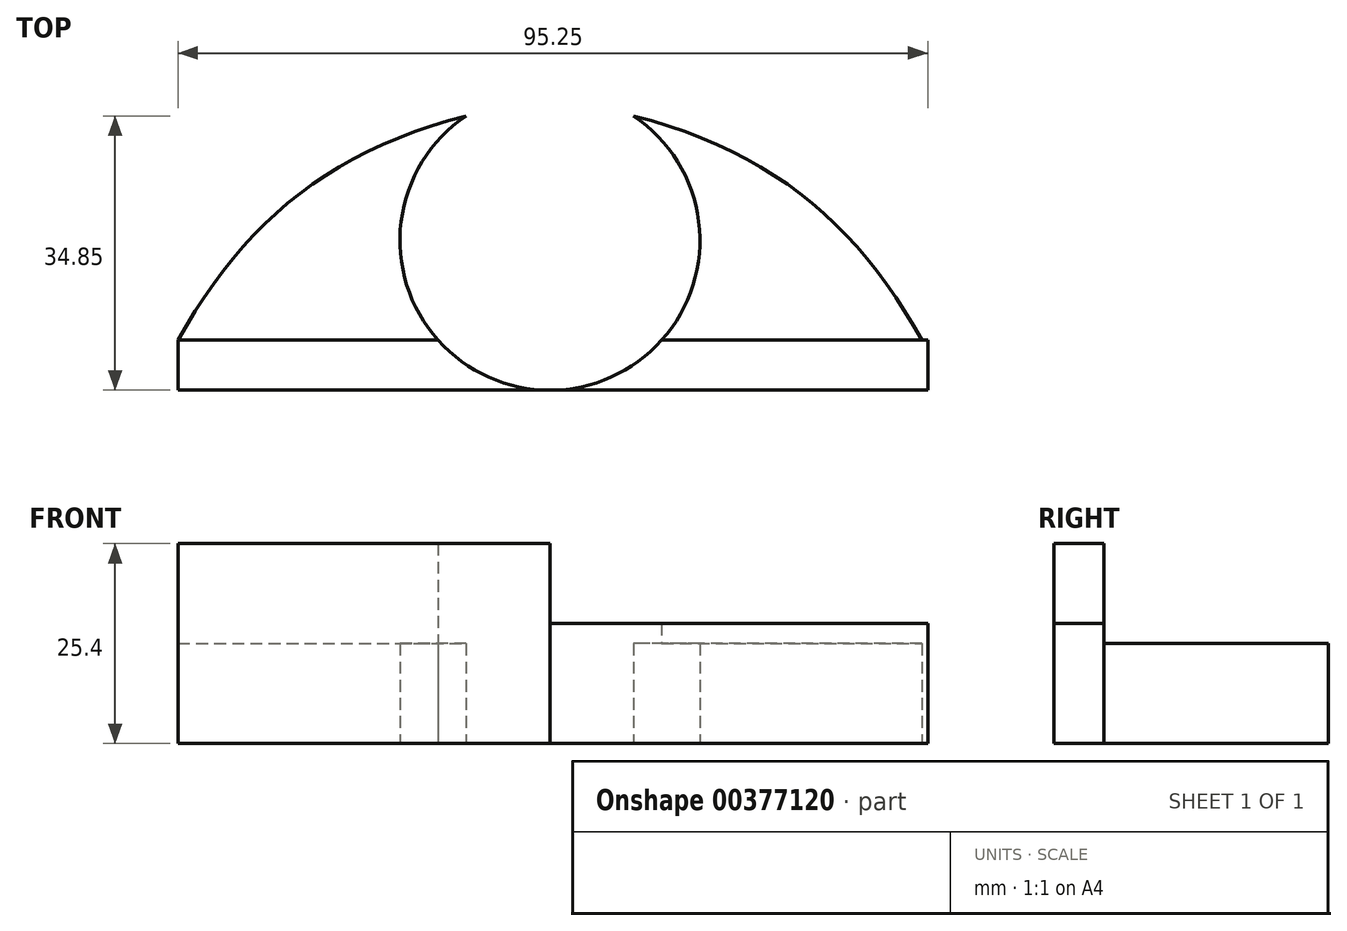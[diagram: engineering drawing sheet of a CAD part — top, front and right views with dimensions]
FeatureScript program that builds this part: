
annotation { "Feature Type Name" : "Feature", "Feature Type Description" : "" }
export const myFeature = defineFeature(function(context is Context, id is Id, definition is map)
    precondition{}
    {
        {
            var Q0;
            Q0=qCreatedBy(makeId("Top.planeOp"),FACE);
            var sketch = newSketch(context, id + "F0", { "sketchPlane" : qUnion([Q0])});
            skArc(sketch, "E0", {"start": v(-10.64, 15.8) * mm, "mid": v(0, -19.05) * mm, "end": v(10.64, 15.8) * mm});
            skLineSegment(sketch, "E1.bottom", {"start": v(-47.24, -12.7) * mm, "end": v(-14.2, -12.7) * mm});
            skLineSegment(sketch, "E1.top", {"start": v(-47.24, -19.05) * mm, "end": v(0, -19.05) * mm});
            skLineSegment(sketch, "E1.left", {"start": v(-47.24, -12.7) * mm, "end": v(-47.24, -19.05) * mm});
            skLineSegment(sketch, "E1.right", {"start": v(48.01, -12.7) * mm, "end": v(48.01, -19.05) * mm});
            skLineSegment(sketch, "E2.trimOffspring", {"start": v(14.2, -12.7) * mm, "end": v(48.01, -12.7) * mm});
            skLineSegment(sketch, "E3", {"start": v(0, -19.05) * mm, "end": v(48.01, -19.05) * mm});
            skLineSegment(sketch, "E4", {"start": v(-29.77, 12.78) * mm, "end": v(29.48, 12.78) * mm, "construction": true});
            skLineSegment(sketch, "E5", {"start": v(0, -23.19) * mm, "end": v(0, 34.86) * mm, "construction": true});
            skFitSpline(sketch, "E6", {"points": [v(-47.24, -12.7) * mm, v(-10.64, 15.8) * mm], "startDerivative": vector(24.24, 43.74) * mm, "endDerivative": vector(52.98, 13.61) * mm});
            skFitSpline(sketch, "E7.MirrorCS", {"points": [v(47.24, -12.7) * mm, v(10.64, 15.8) * mm], "startDerivative": vector(-24.24, 43.74) * mm, "endDerivative": vector(-52.98, 13.61) * mm});
            skLineSegment(sketch, "E8.bottom", {"start": v(-47.24, -19.05) * mm, "end": v(-104, -19.05) * mm});
            skLineSegment(sketch, "E8.top", {"start": v(-47.24, -12.5) * mm, "end": v(-104, -12.5) * mm});
            skLineSegment(sketch, "E8.left", {"start": v(-47.24, -19.05) * mm, "end": v(-47.24, -12.5) * mm});
            skLineSegment(sketch, "E8.right", {"start": v(-104, -19.05) * mm, "end": v(-104, -12.5) * mm});
            skSolve(sketch);
        }
        {
            var Q0;
            {var subQ0=sQuery(id+"F0.wireOp",EDGE,"E7.MirrorCS");Q0=makeQuery(id+"F0.imprint","IMPRINT",FACE,{"disambiguationData":[TD([[makeQuery(id+"F0.imprint","IMPRINT",EDGE,{"derivedFrom":subQ0}),1.0]])]});}
            var Q1;
            {var subQ2=sQuery(id+"F0.wireOp",EDGE,"E1.bottom");Q1=makeQuery(id+"F0.imprint","IMPRINT",FACE,{"disambiguationData":[TD([[makeQuery(id+"F0.imprint","IMPRINT",EDGE,{"derivedFrom":subQ2}),1.0]])]});}
            extrude(context, id + "F1", {"entities" : qUnion([Q0, Q1]), "depth" : 12.7 * mm});
        }
        {
            var Q0;
            {var subQ0=sQuery(id+"F0.wireOp",EDGE,"E1.bottom");Q0=makeQuery(id+"F0.imprint","IMPRINT",FACE,{"disambiguationData":[TD([[makeQuery(id+"F0.imprint","IMPRINT",EDGE,{"derivedFrom":subQ0}),-1.0]])]});}
            extrude(context, id + "F2", {"entities" : qUnion([Q0]), "depth" : 25.4 * mm});
        }
        {
            var Q0;
            {var subQ1=sQuery(id+"F0.wireOp",EDGE,"E1.right");Q0=makeQuery(id+"F0.imprint","IMPRINT",FACE,{"disambiguationData":[TD([[makeQuery(id+"F0.imprint","IMPRINT",EDGE,{"derivedFrom":subQ1}),-1.0]])]});}
            extrude(context, id + "F3", {"entities" : qUnion([Q0]), "operationType" : NewBodyOperationType.ADD, "depth" : 15.24 * mm});
        }
    });
